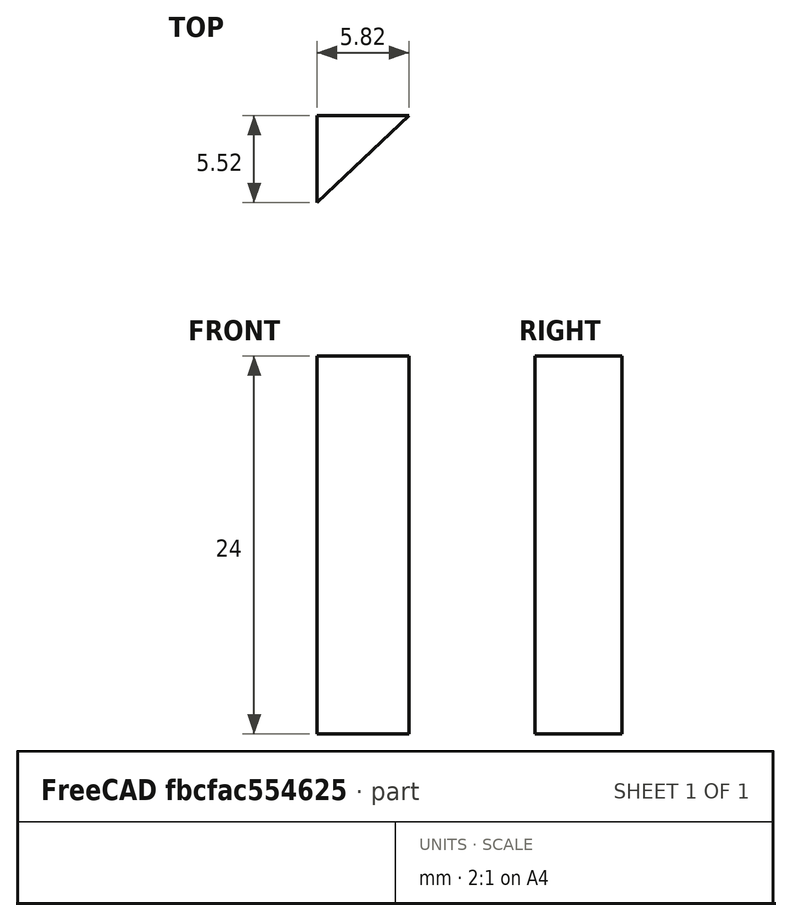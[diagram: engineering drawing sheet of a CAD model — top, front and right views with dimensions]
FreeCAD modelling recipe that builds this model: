
FCSTD DOCUMENT  (FreeCAD 0.17R13528 (Git))
Label: prism
License: All rights reserved
LicenseURL: http://en.wikipedia.org/wiki/All_rights_reserved
objects: Sketcher::SketchObject×1, PartDesign::Pad×1, PartDesign::Draft×1, PartDesign::Body×1
note: 5 computed .brp shape members not serialized (recipe doc carries the construction recipe); baked Part::Feature solids carry a one-line shape summary decoded from their .brp

FEATURE [Sketcher::SketchObject] Sketch
  MapMode = 5
  Support = -> [XY_Plane]
  sketch-geometry (12):
    g0: LineSegment StartX=0 StartY=5.52 StartZ=0 EndX=0 EndY=0 EndZ=0
    g1: LineSegment StartX=0 StartY=0 StartZ=0 EndX=5.52 EndY=5.52 EndZ=0
    g2: LineSegment StartX=5.52 StartY=5.52 StartZ=0 EndX=0 EndY=5.52 EndZ=0
    g3: GeomPoint X=0 Y=0 Z=0
    g4: GeomPoint X=0 Y=0 Z=0
    g5: GeomPoint X=0 Y=0 Z=0
    g6: GeomPoint X=0 Y=0 Z=0
    g7: GeomPoint X=0 Y=0 Z=0
    g8: GeomPoint X=0 Y=0 Z=0
    g9: GeomPoint X=0 Y=0 Z=0
    g10: GeomPoint X=0 Y=0 Z=0
    g11: GeomPoint X=0 Y=0 Z=0
  constraints (16):
    c: Vertical(g0)
    c: Coincident(g0,g1)
    c: Coincident(g1,g2)
    c: Coincident(g2,g0)
    c: Horizontal(g2)
    c: DistanceY(g0,g0) = 5.52
    c: DistanceX(g2,g2) = 5.52
    c: Coincident(g3,g0)
    c: Coincident(g4,g-1)
    c: Coincident(g5,g-1)
    c: Coincident(g6,g-1)
    c: Coincident(g7,g0)
    c: Coincident(g8,g-1)
    c: Coincident(g10,g0)
    c: Coincident(g11,g-1)
    c: Coincident(g-1,g0)
FEATURE [PartDesign::Pad] Pad
  Length = 24
  Length2 = 100
  Midplane = true
  Profile = -> Sketch
  Type = 0
FEATURE [PartDesign::Draft] Draft
  Angle = 1.5
  Base = -> Pad [Face2]
  BaseFeature = -> Pad
  Reversed = true
FEATURE [PartDesign::Body] Body
  Group = -> [Sketch,Pad,Draft]
  Origin = -> Origin
  Tip = -> Draft
